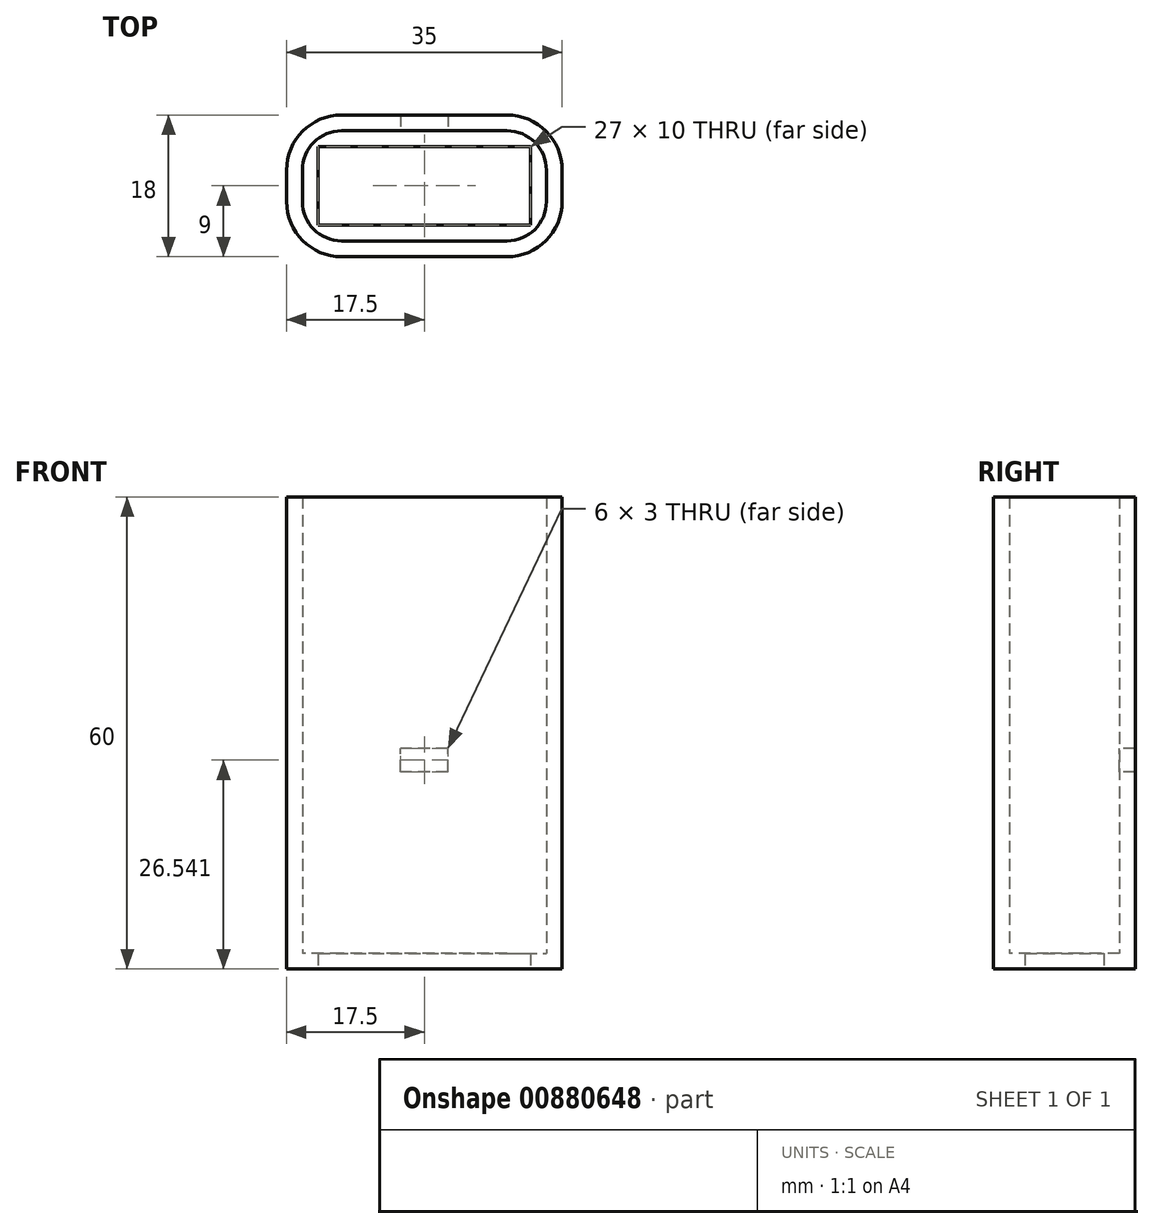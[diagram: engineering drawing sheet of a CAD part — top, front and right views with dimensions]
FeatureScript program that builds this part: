
annotation { "Feature Type Name" : "Feature", "Feature Type Description" : "" }
export const myFeature = defineFeature(function(context is Context, id is Id, definition is map)
    precondition{}
    {
        {
            var Q0;
            Q0=qCreatedBy(makeId("Top.planeOp"),FACE);
            var sketch = newSketch(context, id + "F0", { "sketchPlane" : qUnion([Q0])});
            skLineSegment(sketch, "E0.bottom", {"start": v(5, 0) * mm, "end": v(26, 0) * mm});
            skLineSegment(sketch, "E0.top", {"start": v(5, 14) * mm, "end": v(26, 14) * mm});
            skLineSegment(sketch, "E0.left", {"start": v(0, 5) * mm, "end": v(0, 9) * mm});
            skLineSegment(sketch, "E0.right", {"start": v(31, 5) * mm, "end": v(31, 9) * mm});
            skPoint(sketch, "E1.visualSharp", {"position": v(0, 14) * mm});
            skArc(sketch, "E1.filletArc", {"start": v(5, 14) * mm, "mid": v(1.46, 12.54) * mm, "end": v(0, 9) * mm});
            skPoint(sketch, "E2.visualSharp", {"position": v(0, 0) * mm});
            skArc(sketch, "E2.filletArc", {"start": v(0, 5) * mm, "mid": v(1.46, 1.46) * mm, "end": v(5, 0) * mm});
            skPoint(sketch, "E3.visualSharp", {"position": v(31, 14) * mm});
            skArc(sketch, "E3.filletArc", {"start": v(31, 9) * mm, "mid": v(29.54, 12.54) * mm, "end": v(26, 14) * mm});
            skPoint(sketch, "E4.visualSharp", {"position": v(31, 0) * mm});
            skArc(sketch, "E4.filletArc", {"start": v(26, 0) * mm, "mid": v(29.54, 1.46) * mm, "end": v(31, 5) * mm});
            skArc(sketch, "E5.0", {"start": v(5, 16) * mm, "mid": v(0.05, 13.95) * mm, "end": v(-2, 9) * mm});
            skLineSegment(sketch, "E5.1", {"start": v(-2, 5) * mm, "end": v(-2, 9) * mm});
            skLineSegment(sketch, "E5.2", {"start": v(5, 16) * mm, "end": v(26, 16) * mm});
            skArc(sketch, "E5.3", {"start": v(-2, 5) * mm, "mid": v(0.05, 0.05) * mm, "end": v(5, -2) * mm});
            skArc(sketch, "E5.4", {"start": v(33, 9) * mm, "mid": v(30.95, 13.95) * mm, "end": v(26, 16) * mm});
            skLineSegment(sketch, "E5.5", {"start": v(33, 5) * mm, "end": v(33, 9) * mm});
            skArc(sketch, "E5.6", {"start": v(26, -2) * mm, "mid": v(30.95, 0.05) * mm, "end": v(33, 5) * mm});
            skLineSegment(sketch, "E5.7", {"start": v(5, -2) * mm, "end": v(26, -2) * mm});
            skLineSegment(sketch, "E6.0", {"start": v(2, 12) * mm, "end": v(29, 12) * mm});
            skLineSegment(sketch, "E6.1", {"start": v(2, 2) * mm, "end": v(2, 12) * mm});
            skLineSegment(sketch, "E6.2", {"start": v(2, 2) * mm, "end": v(29, 2) * mm});
            skLineSegment(sketch, "E6.3", {"start": v(29, 2) * mm, "end": v(29, 12) * mm});
            skSolve(sketch);
        }
        {
            var Q0;
            Q0=makeQuery(id+"F0.imprint","IMPRINT",FACE,{"disambiguationData":[TD([[makeQuery(id+"F0.imprint","IMPRINT",EDGE,{"derivedFrom":sQuery(id+"F0.wireOp",EDGE,"E0.bottom")}),1.0]])]});
            var Q1;
            Q1=makeQuery(id+"F0.imprint","IMPRINT",FACE,{"disambiguationData":[TD([[makeQuery(id+"F0.imprint","IMPRINT",EDGE,{"derivedFrom":sQuery(id+"F0.wireOp",EDGE,"E0.bottom")}),-1.0]])]});
            extrude(context, id + "F1", {"entities" : qUnion([Q0, Q1]), "depth" : 2 * mm, "offsetDistance" : 25 * mm});
        }
        {
            var Q0;
            Q0=makeQuery(id+"F0.imprint","IMPRINT",FACE,{"disambiguationData":[TD([[makeQuery(id+"F0.imprint","IMPRINT",EDGE,{"derivedFrom":sQuery(id+"F0.wireOp",EDGE,"E0.bottom")}),-1.0]])]});
            extrude(context, id + "F2", {"entities" : qUnion([Q0]), "operationType" : NewBodyOperationType.ADD, "depth" : 60 * mm, "offsetDistance" : 25 * mm});
        }
        {
            var Q0;
            Q0=qCreatedBy(makeId("Front.planeOp"),FACE);
            var sketch = newSketch(context, id + "F3", { "sketchPlane" : qUnion([Q0])});
            skLineSegment(sketch, "E7.bottom", {"start": v(12.5, 28.04) * mm, "end": v(18.5, 28.04) * mm});
            skLineSegment(sketch, "E7.top", {"start": v(12.5, 25.04) * mm, "end": v(18.5, 25.04) * mm});
            skLineSegment(sketch, "E7.left", {"start": v(12.5, 28.04) * mm, "end": v(12.5, 25.04) * mm});
            skLineSegment(sketch, "E7.right", {"start": v(18.5, 28.04) * mm, "end": v(18.5, 25.04) * mm});
            skSolve(sketch);
        }
        {
            var Q0;
            Q0=makeQuery(id+"F3.imprint","IMPRINT",FACE,{"disambiguationData":[TD([[makeQuery(id+"F3.imprint","IMPRINT",EDGE,{"derivedFrom":sQuery(id+"F3.wireOp",EDGE,"E7.bottom")}),-1.0]])]});
            extrude(context, id + "F4", {"entities" : qUnion([Q0]), "operationType" : NewBodyOperationType.REMOVE, "oppositeDirection" : true, "depth" : 25 * mm, "offsetDistance" : 25 * mm});
        }
    });
